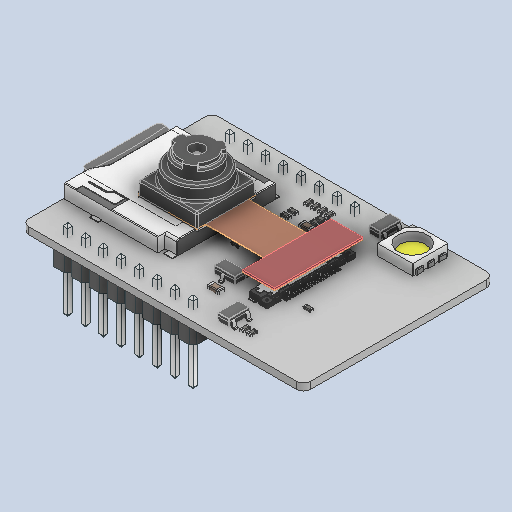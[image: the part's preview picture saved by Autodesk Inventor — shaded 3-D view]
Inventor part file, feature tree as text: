
AUTODESK INVENTOR PART (.ipt)
format: ipt  version: 2022 (Build 260153000, 153)  size: 5,102,592 bytes
history: native  units: mm
features: other x109, fillet x1
ambient origin geometry x8: Origin, YZ Plane, XZ Plane, XY Plane, X Axis, Y Axis, Z Axis, Center Point
bodies: Volumenkörper1 (feature_tree), Volumenkörper2 (feature_tree), Volumenkörper3 (feature_tree), Volumenkörper4 (feature_tree), Volumenkörper5 (feature_tree), Volumenkörper6 (feature_tree), Volumenkörper7 (feature_tree), Volumenkörper8 (feature_tree), Volumenkörper9 (feature_tree), Volumenkörper10 (feature_tree), Volumenkörper11 (feature_tree), Volumenkörper12 (feature_tree), Volumenkörper13 (feature_tree), Volumenkörper14 (feature_tree), Volumenkörper15 (feature_tree), Volumenkörper16 (feature_tree), Volumenkörper17 (feature_tree), Volumenkörper18 (feature_tree), Volumenkörper19 (feature_tree), Volumenkörper20 (feature_tree), Volumenkörper21 (feature_tree), Volumenkörper22 (feature_tree), Volumenkörper23 (feature_tree), Volumenkörper24 (feature_tree), Volumenkörper25 (feature_tree), Volumenkörper26 (feature_tree), Volumenkörper27 (feature_tree), Volumenkörper28 (feature_tree), Volumenkörper29 (feature_tree), Volumenkörper30 (feature_tree), Volumenkörper31 (feature_tree), Volumenkörper32 (feature_tree), Volumenkörper33 (feature_tree), Volumenkörper34 (feature_tree), Volumenkörper35 (feature_tree), Volumenkörper36 (feature_tree), Volumenkörper37 (feature_tree), Volumenkörper38 (feature_tree), Volumenkörper39 (feature_tree), Volumenkörper40 (feature_tree), Volumenkörper41 (feature_tree), Volumenkörper42 (feature_tree), Volumenkörper43 (feature_tree), Volumenkörper44 (feature_tree), Volumenkörper45 (feature_tree), Volumenkörper46 (feature_tree), Volumenkörper47 (feature_tree), Volumenkörper48 (feature_tree), Volumenkörper49 (feature_tree), Volumenkörper50 (feature_tree), Volumenkörper51 (feature_tree), Volumenkörper52 (feature_tree), Volumenkörper53 (feature_tree), Volumenkörper54 (feature_tree), Volumenkörper55 (feature_tree), Volumenkörper56 (feature_tree), Volumenkörper57 (feature_tree), Volumenkörper58 (feature_tree), Volumenkörper59 (feature_tree), Volumenkörper60 (feature_tree), Volumenkörper61 (feature_tree), Volumenkörper62 (feature_tree), Volumenkörper63 (feature_tree), Volumenkörper64 (feature_tree), Volumenkörper65 (feature_tree), Volumenkörper66 (feature_tree), Volumenkörper67 (feature_tree), Volumenkörper68 (feature_tree), Volumenkörper69 (feature_tree), Volumenkörper70 (feature_tree), Volumenkörper71 (feature_tree), Volumenkörper72 (feature_tree), Volumenkörper73 (feature_tree), Volumenkörper74 (feature_tree), Volumenkörper75 (feature_tree), Volumenkörper76 (feature_tree), Volumenkörper77 (feature_tree), Volumenkörper78 (feature_tree), Volumenkörper79 (feature_tree), Volumenkörper80 (feature_tree), Volumenkörper81 (feature_tree), Volumenkörper82 (feature_tree), Volumenkörper83 (feature_tree), Volumenkörper84 (feature_tree), Volumenkörper85 (feature_tree), Volumenkörper86 (feature_tree), Volumenkörper87 (feature_tree), Volumenkörper88 (feature_tree), Volumenkörper89 (feature_tree), Volumenkörper90 (feature_tree), Volumenkörper91 (feature_tree), Volumenkörper92 (feature_tree), Volumenkörper93 (feature_tree), Volumenkörper94 (feature_tree), Volumenkörper95 (feature_tree), Volumenkörper96 (feature_tree), Volumenkörper97 (feature_tree), Volumenkörper98 (feature_tree), Volumenkörper99 (feature_tree), Volumenkörper100 (feature_tree), Volumenkörper101 (feature_tree), Volumenkörper102 (feature_tree), Volumenkörper103 (feature_tree), Volumenkörper104 (feature_tree), Volumenkörper105 (feature_tree), Volumenkörper106 (feature_tree), Volumenkörper107 (feature_tree), Volumenkörper108 (feature_tree), Volumenkörper109 (feature_tree), Volumenkörper110 (feature_tree), Volumenkörper111 (feature_tree), Body1 (feature_tree)
feature tree (110):
  other  "Pin Header 4 x 1 TH 2.54mm Pitch v1_1:1"
  other  "Pin Header 4 x 1 TH 2.54mm Pitch v1_1:2"
  other  "Pin Header 4 x 1 TH 2.54mm Pitch v1_1:3"
  other  "Pin Header 4 x 1 TH 2.54mm Pitch v1_1:4"
  other  "Pin Header 4 x 1 TH 2.54mm Pitch v1_1:5"
  other  "Pin Header 4 x 1 TH 2.54mm Pitch v1_1:6"
  other  "Pin Header 4 x 1 TH 2.54mm Pitch v1_1:7"
  other  "Pin Header 4 x 1 TH 2.54mm Pitch v1_1:8"
  other  "Pin Header 4 x 1 TH 2.54mm Pitch v1_2:1"
  other  "Pin Header 4 x 1 TH 2.54mm Pitch v1_2:2"
  other  "Pin Header 4 x 1 TH 2.54mm Pitch v1_2:3"
  other  "Pin Header 4 x 1 TH 2.54mm Pitch v1_2:4"
  other  "Pin Header 4 x 1 TH 2.54mm Pitch v1_2:5"
  other  "Pin Header 4 x 1 TH 2.54mm Pitch v1_2:6"
  other  "Pin Header 4 x 1 TH 2.54mm Pitch v1_2:7"
  other  "Pin Header 4 x 1 TH 2.54mm Pitch v1_2:8"
  other  "Pin Header 4 x 1 TH 2.54mm Pitch v1_3:1"
  other  "Pin Header 4 x 1 TH 2.54mm Pitch v1_3:2"
  other  "Pin Header 4 x 1 TH 2.54mm Pitch v1_3:3"
  other  "Pin Header 4 x 1 TH 2.54mm Pitch v1_3:4"
  other  "Pin Header 4 x 1 TH 2.54mm Pitch v1_3:5"
  other  "Pin Header 4 x 1 TH 2.54mm Pitch v1_3:6"
  other  "Pin Header 4 x 1 TH 2.54mm Pitch v1_3:7"
  other  "Pin Header 4 x 1 TH 2.54mm Pitch v1_3:8"
  other  "Pin Header 4 x 1 TH 2.54mm Pitch v1_4:1"
  other  "Pin Header 4 x 1 TH 2.54mm Pitch v1_4:2"
  other  "Pin Header 4 x 1 TH 2.54mm Pitch v1_4:3"
  other  "Pin Header 4 x 1 TH 2.54mm Pitch v1_4:4"
  other  "Pin Header 4 x 1 TH 2.54mm Pitch v1_4:5"
  other  "Pin Header 4 x 1 TH 2.54mm Pitch v1_4:6"
  other  "Pin Header 4 x 1 TH 2.54mm Pitch v1_4:7"
  other  "Pin Header 4 x 1 TH 2.54mm Pitch v1_4:8"
  other  "u_1:1"
  other  "u_1:2"
  other  "u_1:3"
  other  "u_1:4"
  other  "u_1:5"
  other  "capacitor-CAPM-TANTB-YL v1_1:1"
  other  "capacitor-CAPM-TANTB-YL v1_1:2"
  other  "capacitor-CAPM-TANTB-YL v1_1:3"
  other  "switch-3x4x2mm - 2 Pad v1_1:1"
  other  "nano - reg_1:1"
  other  "icbody_1:1"
  other  "Component5_1:1"
  other  "Component5_2:1"
  other  "Component5_3:1"
  other  "Component5_4:1"
  other  "Component5(Mirror)_1:1"
  other  "Component5(Mirror)_2:1"
  other  "Component5(Mirror)_3:1"
  other  "Component5(Mirror)_4:1"
  other  "Fusion_1:1"
  fillet  "Fillet_1:1"  [1 undecoded]
  other  "resistor-NTC-0402-T0.6 v1_1:1"
  other  "resistor-NTC-0402-T0.6 v1_2:1"
  other  "resistor-NTC-0402-T0.6 v1_3:1"
  other  "resistor-NTC-0805-T1.3 v1_1:1"
  other  "resistor-NTC-0402-T0.6 v1_4:1"
  other  "resistor-NTC-0402-T0.6 v1_5:1"
  other  "resistor-NTC-0402-T0.6 v1_6:1"
  other  "resistor-NTC-0402-T0.6 v1_7:1"
  other  "smd-transistor-SOT23-3 v1_1:1"
  other  "smd-transistor-SOT23-3 v1_1:2"
  other  "smd-transistor-SOT23-3 v1_1:3"
  other  "smd-transistor-SOT23-3 v1_1:4"
  other  "smd-transistor-SOT23-3 v1_2:1"
  other  "smd-transistor-SOT23-3 v1_2:2"
  other  "smd-transistor-SOT23-3 v1_2:3"
  other  "smd-transistor-SOT23-3 v1_2:4"
  other  "resistor-NTC-0402-T0.6 v1_8:1"
  other  "resistor-NTC-0402-T0.6 v1_9:1"
  other  "resistor-NTC-0402-T0.6 v1_10:1"
  other  "LED SMD 5050 White v1_1:1"
  other  "resistor-NTC-0402-T0.6 v1_11:1"
  other  "resistor-NTC-0402-T0.6 v1_12:1"
  other  "resistor-NTC-0402-T0.6 v1_13:1"
  other  "resistor-NTC-0402-T0.6 v1_14:1"
  other  "resistor-NTC-0402-T0.6 v1_15:1"
  other  "resistor-NTC-0402-T0.6 v1_16:1"
  other  "resistor-NTC-0402-T0.6 v1_17:1"
  other  "capacitor-CAPC-0603-T0.9-BN v1_1:1"
  other  "resistor-NTC-0402-T0.6 v1_18:1"
  other  "capacitor-CAPC-0603-T0.9-BN v1_2:1"
  other  "smd-transistor-SOT23-3 v1_3:1"
  other  "smd-transistor-SOT23-3 v1_3:2"
  other  "smd-transistor-SOT23-3 v1_3:3"
  other  "smd-transistor-SOT23-3 v1_3:4"
  other  "connector smd usl00-20l_p0-4_l12-6_w2-75 v1_1:1"
  other  "resistor-NTC-0402-T0.6 v1_19:1"
  other  "resistor-NTC-0402-T0.6 v1_20:1"
  other  "smd-transistor-SOT23-3 v1_4:1"
  other  "smd-transistor-SOT23-3 v1_4:2"
  other  "smd-transistor-SOT23-3 v1_4:3"
  other  "smd-transistor-SOT23-3 v1_4:4"
  other  "sdreader_1:1"
  other  "Micro SD-Card v1_1:1"
  other  "Micro SD-Card v1_1:2"
  other  "Micro SD-Card v1_1:3"
  other  "Micro SD-Card v1_1:4"
  other  "Micro SD-Card v1_1:5"
  other  "Micro SD-Card v1_1:6"
  other  "Micro SD-Card v1_1:7"
  other  "Micro SD-Card v1_1:8"
  other  "Micro SD-Card v1_1:9"
  other  "User Library-ov9655_ov9655_flex_pcb_1:1"
  other  "User Library-ov9655_ov9655_flex_reinf_1:1"
  other  "User Library-ov9655_ov9655_back_panel_1:1"
  other  "User Library-ov9655_ov9655_body_1:1"
  other  "User Library-ov9655_ov9655_lens_1:1"
  other  "Body1:1"
note: 1 required parameter value undecoded (feature->parameter linkage not recoverable at this tier; creation-order binding heuristic only, values carry confidence <= 0.55)
